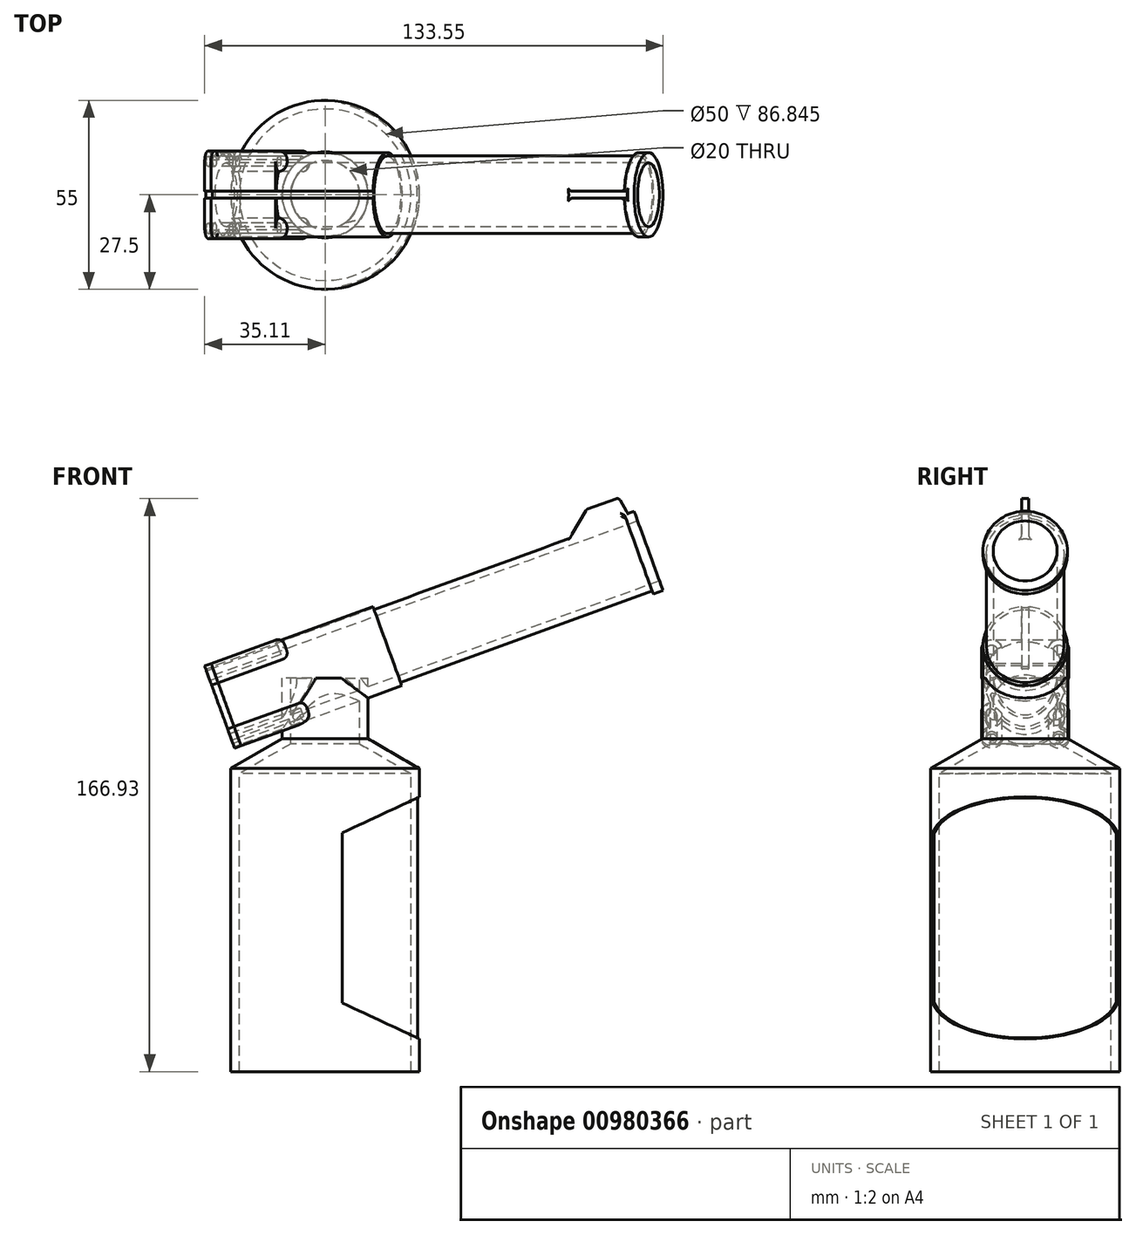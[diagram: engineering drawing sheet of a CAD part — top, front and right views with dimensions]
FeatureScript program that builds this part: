
annotation { "Feature Type Name" : "Feature", "Feature Type Description" : "" }
export const myFeature = defineFeature(function(context is Context, id is Id, definition is map)
    precondition{}
    {
        {
            var Q0;
            Q0=qCreatedBy(makeId("Front.planeOp"),FACE);
            var sketch = newSketch(context, id + "F0", { "sketchPlane" : qUnion([Q0])});
            skLineSegment(sketch, "E0", {"start": v(0, 0) * mm, "end": v(88.33, 32.15) * mm, "construction": true});
            skLineSegment(sketch, "E1", {"start": v(0, 151.2) * mm, "end": v(0, -135.9) * mm, "construction": true});
            skLineSegment(sketch, "E2", {"start": v(-3.08, 8.46) * mm, "end": v(85.25, 40.6) * mm, "construction": true});
            skLineSegment(sketch, "E3", {"start": v(85.25, 40.6) * mm, "end": v(91.4, 23.7) * mm, "construction": true});
            skLineSegment(sketch, "E4", {"start": v(91.4, 23.7) * mm, "end": v(3.08, -8.46) * mm, "construction": true});
            skLineSegment(sketch, "E5", {"start": v(3.08, -8.46) * mm, "end": v(-3.08, 8.46) * mm, "construction": true});
            skLineSegment(sketch, "E6", {"start": v(-52.04, -9.05) * mm, "end": v(68.24, 34.73) * mm});
            skLineSegment(sketch, "E7.0", {"start": v(-5.74, 9.93) * mm, "end": v(67.55, 36.61) * mm});
            skLineSegment(sketch, "E8", {"start": v(67.55, 36.61) * mm, "end": v(68.24, 34.73) * mm, "construction": true});
            skLineSegment(sketch, "E9", {"start": v(68.24, 34.73) * mm, "end": v(67.2, 37.55) * mm});
            skLineSegment(sketch, "E10", {"start": v(67.2, 37.55) * mm, "end": v(70.03, 38.58) * mm});
            skLineSegment(sketch, "E11", {"start": v(70.03, 38.58) * mm, "end": v(71.05, 35.76) * mm});
            skLineSegment(sketch, "E12", {"start": v(71.05, 35.76) * mm, "end": v(68.24, 34.73) * mm});
            skLineSegment(sketch, "E13", {"start": v(-5.74, 9.93) * mm, "end": v(-6.09, 10.87) * mm});
            skLineSegment(sketch, "E14", {"start": v(-6.09, 10.87) * mm, "end": v(-53.07, -6.23) * mm});
            skLineSegment(sketch, "E15", {"start": v(-53.07, -6.23) * mm, "end": v(-52.04, -9.05) * mm});
            skSolve(sketch);
        }
        {
            var Q0;
            Q0 = qSketchRegion(id + "F0", true);
            var Q1;
            Q1=sQuery(id+"F0.wireOp",EDGE,"E0");
            revolve(context, id + "F1", {"surfaceOperationType" : NewSurfaceOperationType.NEW, "entities" : qUnion([Q0]), "axis" : qUnion([Q1]), "revolveType" : RevolveType.FULL});
        }
        {
            var Q0;
            Q0=makeQuery(id+"F1.opRevolve","SWEPT_FACE",FACE,{"disambiguationData":[OSD([sQuery(id+"F0.wireOp",EDGE,"E15")])]});
            var sketch = newSketch(context, id + "F2", { "sketchPlane" : qUnion([Q0])});
            skCircle(sketch, "E16", {"center": v(-9.76, -9.76) * mm, "radius": 3 * mm});
            skCircle(sketch, "E17", {"center": v(9.76, -9.76) * mm, "radius": 3 * mm});
            skCircle(sketch, "E18", {"center": v(9.76, 9.76) * mm, "radius": 3 * mm});
            skCircle(sketch, "E19", {"center": v(-9.76, 9.76) * mm, "radius": 3 * mm});
            skLineSegment(sketch, "E20.bottom", {"start": v(-9.76, 9.76) * mm, "end": v(9.76, 9.76) * mm, "construction": true});
            skLineSegment(sketch, "E20.top", {"start": v(-9.76, -9.76) * mm, "end": v(9.76, -9.76) * mm, "construction": true});
            skLineSegment(sketch, "E20.left", {"start": v(-9.76, 9.76) * mm, "end": v(-9.76, -9.76) * mm, "construction": true});
            skLineSegment(sketch, "E20.right", {"start": v(9.76, 9.76) * mm, "end": v(9.76, -9.76) * mm, "construction": true});
            skCircle(sketch, "E21", {"center": v(0, 0) * mm, "radius": 10.8 * mm, "construction": true});
            skLineSegment(sketch, "E22", {"start": v(0, 12.3) * mm, "end": v(0, 9.3) * mm, "construction": true});
            skLineSegment(sketch, "E23", {"start": v(-9.76, 9.76) * mm, "end": v(9.76, -9.76) * mm, "construction": true});
            skCircle(sketch, "E24", {"center": v(-9.76, 9.76) * mm, "radius": 1.5 * mm});
            skCircle(sketch, "E25", {"center": v(-9.76, -9.76) * mm, "radius": 1.5 * mm});
            skCircle(sketch, "E26", {"center": v(9.76, -9.76) * mm, "radius": 1.5 * mm});
            skCircle(sketch, "E27", {"center": v(9.76, 9.76) * mm, "radius": 1.5 * mm});
            skLineSegment(sketch, "E28", {"start": v(-9.76, 12.76) * mm, "end": v(9.76, 12.76) * mm});
            skArc(sketch, "E29", {"start": v(7.64, 7.64) * mm, "mid": v(0, 10.8) * mm, "end": v(-7.64, 7.64) * mm});
            skSolve(sketch);
        }
        {
            var Q0;
            Q0 = qSketchRegion(id + "F2", true);
            extrude(context, id + "F3", {"entities" : qUnion([Q0]), "operationType" : NewBodyOperationType.ADD, "oppositeDirection" : true, "depth" : 20 * mm, "offsetDistance" : 25 * mm});
        }
        {
            var Q0;
            Q0=makeQuery(id+"F3.opExtrude","CAP_FACE",FACE,{"disambiguationData":[OSD([sQuery(id+"F2.wireOp",EDGE,"E18"),sQuery(id+"F2.wireOp",EDGE,"E19"),sQuery(id+"F2.wireOp",EDGE,"E24"),sQuery(id+"F2.wireOp",EDGE,"E27"),sQuery(id+"F2.wireOp",EDGE,"E28"),sQuery(id+"F2.wireOp",EDGE,"E29")])],"isStart":false});
            var sketch = newSketch(context, id + "F4", { "sketchPlane" : qUnion([Q0])});
            skCircle(sketch, "E30", {"center": v(-9.76, 9.76) * mm, "radius": 3 * mm});
            skCircle(sketch, "E31", {"center": v(9.76, 9.76) * mm, "radius": 3 * mm});
            skCircle(sketch, "E32", {"center": v(9.76, -9.76) * mm, "radius": 3 * mm});
            skCircle(sketch, "E33", {"center": v(-9.76, -9.76) * mm, "radius": 3 * mm});
            skSolve(sketch);
        }
        {
            var Q0;
            Q0 = qSketchRegion(id + "F4", true);
            extrude(context, id + "F5", {"entities" : qUnion([Q0]), "operationType" : NewBodyOperationType.ADD, "depth" : 2 * mm, "offsetDistance" : 25 * mm});
        }
        {
            var Q0;
            Q0=makeQuery(id+"F5.opExtrude","CAP_EDGE",EDGE,{"disambiguationData":[OSD([sQuery(id+"F4.wireOp",EDGE,"E31")])],"isStart":false});
            var Q1;
            Q1=makeQuery(id+"F5.opExtrude","CAP_EDGE",EDGE,{"disambiguationData":[OSD([sQuery(id+"F4.wireOp",EDGE,"E30")])],"isStart":false});
            var Q2;
            Q2=makeQuery(id+"F5.opExtrude","CAP_EDGE",EDGE,{"disambiguationData":[OSD([sQuery(id+"F4.wireOp",EDGE,"E33")])],"isStart":false});
            var Q3;
            Q3=makeQuery(id+"F5.opExtrude","CAP_EDGE",EDGE,{"disambiguationData":[OSD([sQuery(id+"F4.wireOp",EDGE,"E32")])],"isStart":false});
            fillet(context, id + "F6", {"entities" : qUnion([Q0, Q1, Q2, Q3]), "radius" : 2 * mm, "tangentPropagation" : true, "allowEdgeOverflow" : false});
        }
        {
            var Q0;
            Q0=makeQuery(id+"F3.boolean.opBoolean","MERGE",FACE,{"derivedFrom":[makeQuery(id+"F1.opRevolve","SWEPT_FACE",FACE,{"disambiguationData":[OSD([sQuery(id+"F0.wireOp",EDGE,"E15")])]}),makeQuery(id+"F3.opExtrude","CAP_FACE",FACE,{"disambiguationData":[OSD([sQuery(id+"F2.wireOp",EDGE,"E16"),sQuery(id+"F2.wireOp",EDGE,"E25")])],"isStart":true}),makeQuery(id+"F3.opExtrude","CAP_FACE",FACE,{"disambiguationData":[OSD([sQuery(id+"F2.wireOp",EDGE,"E17"),sQuery(id+"F2.wireOp",EDGE,"E26")])],"isStart":true}),makeQuery(id+"F3.opExtrude","CAP_FACE",FACE,{"disambiguationData":[OSD([sQuery(id+"F2.wireOp",EDGE,"E18"),sQuery(id+"F2.wireOp",EDGE,"E19"),sQuery(id+"F2.wireOp",EDGE,"E24"),sQuery(id+"F2.wireOp",EDGE,"E27"),sQuery(id+"F2.wireOp",EDGE,"E28"),sQuery(id+"F2.wireOp",EDGE,"E29")])],"isStart":true})]});
            var sketch = newSketch(context, id + "F7", { "sketchPlane" : qUnion([Q0])});
            skLineSegment(sketch, "E34.bottom", {"start": v(-1, 12.76) * mm, "end": v(1, 12.76) * mm});
            skLineSegment(sketch, "E34.top", {"start": v(-1, 11.76) * mm, "end": v(1, 11.76) * mm});
            skLineSegment(sketch, "E34.left", {"start": v(-1, 12.76) * mm, "end": v(-1, 11.76) * mm});
            skLineSegment(sketch, "E34.right", {"start": v(1, 12.76) * mm, "end": v(1, 11.76) * mm});
            skLineSegment(sketch, "E35", {"start": v(0, 0) * mm, "end": v(0, 12.76) * mm});
            skSolve(sketch);
        }
        {
            var Q0;
            Q0 = qSketchRegion(id + "F7", true);
            extrude(context, id + "F8", {"entities" : qUnion([Q0]), "operationType" : NewBodyOperationType.REMOVE, "oppositeDirection" : true, "depth" : 50 * mm, "offsetDistance" : 25 * mm});
        }
        {
            var Q0;
            Q0=makeQuery(id+"F8.boolean.opBoolean","INTERSECT",EDGE,{"derivedFrom":[makeQuery(id+"F1.opRevolve","SWEPT_FACE",FACE,{"disambiguationData":[OSD([sQuery(id+"F0.wireOp",EDGE,"E14")])]}),makeQuery(id+"F8.opExtrude","SWEPT_FACE",FACE,{"disambiguationData":[OSD([sQuery(id+"F7.wireOp",EDGE,"E34.right")])]})]});
            var Q1;
            Q1=makeQuery(id+"F8.boolean.opBoolean","COPY",EDGE,{"derivedFrom":makeQuery(id+"F8.opExtrude","SWEPT_EDGE",EDGE,{"disambiguationData":[OSD([sQuery(id+"F7.wireOp",EDGE,"E34.top"),sQuery(id+"F7.wireOp",EDGE,"E34.right")])]})});
            var Q2;
            Q2=makeQuery(id+"F8.boolean.opBoolean","COPY",EDGE,{"derivedFrom":makeQuery(id+"F8.opExtrude","SWEPT_EDGE",EDGE,{"disambiguationData":[OSD([sQuery(id+"F7.wireOp",EDGE,"E34.top"),sQuery(id+"F7.wireOp",EDGE,"E34.left")])]})});
            var Q3;
            Q3=makeQuery(id+"F8.boolean.opBoolean","INTERSECT",EDGE,{"derivedFrom":[makeQuery(id+"F1.opRevolve","SWEPT_FACE",FACE,{"disambiguationData":[OSD([sQuery(id+"F0.wireOp",EDGE,"E14")])]}),makeQuery(id+"F8.opExtrude","SWEPT_FACE",FACE,{"disambiguationData":[OSD([sQuery(id+"F7.wireOp",EDGE,"E34.left")])]})]});
            var Q4;
            Q4=makeQuery(id+"F8.boolean.opBoolean","COPY",EDGE,{"derivedFrom":makeQuery(id+"F8.opExtrude","SWEPT_EDGE",EDGE,{"disambiguationData":[OSD([sQuery(id+"F2.wireOp",EDGE,"E28"),sQuery(id+"F7.wireOp",EDGE,"E34.bottom"),sQuery(id+"F7.wireOp",EDGE,"E34.right")])]})});
            var Q5;
            Q5=makeQuery(id+"F8.boolean.opBoolean","COPY",EDGE,{"derivedFrom":makeQuery(id+"F8.opExtrude","SWEPT_EDGE",EDGE,{"disambiguationData":[OSD([sQuery(id+"F2.wireOp",EDGE,"E28"),sQuery(id+"F7.wireOp",EDGE,"E34.bottom"),sQuery(id+"F7.wireOp",EDGE,"E34.left")])]})});
            fillet(context, id + "F9", {"entities" : qUnion([Q0, Q1, Q2, Q3, Q4, Q5]), "radius" : 0.2 * mm, "tangentPropagation" : true, "allowEdgeOverflow" : false});
        }
        {
            var Q0;
            Q0=qCreatedBy(makeId("Front.planeOp"),FACE);
            var sketch = newSketch(context, id + "F10", { "sketchPlane" : qUnion([Q0])});
            skLineSegment(sketch, "E36", {"start": v(68.07, 38.1) * mm, "end": v(65.54, 42.5) * mm});
            skLineSegment(sketch, "E37", {"start": v(65.54, 42.5) * mm, "end": v(56.14, 39.08) * mm});
            skLineSegment(sketch, "E38", {"start": v(56.14, 39.08) * mm, "end": v(50.97, 30.12) * mm});
            skLineSegment(sketch, "E39", {"start": v(64.7, 43.61) * mm, "end": v(64.7, 37.15) * mm, "construction": true});
            skLineSegment(sketch, "E40", {"start": v(50.97, 30.12) * mm, "end": v(68.98, 36.24) * mm});
            skLineSegment(sketch, "E41", {"start": v(68.98, 36.24) * mm, "end": v(68.07, 38.1) * mm});
            skSolve(sketch);
        }
        {
            var Q0;
            Q0=makeQuery(id+"F10.imprint","IMPRINT",FACE,{"disambiguationData":[TD([[makeQuery(id+"F10.imprint","IMPRINT",EDGE,{"derivedFrom":sQuery(id+"F10.wireOp",EDGE,"E36")}),1.0]])]});
            extrude(context, id + "F11", {"entities" : qUnion([Q0]), "operationType" : NewBodyOperationType.ADD, "endBound" : BoundingType.SYMMETRIC, "depth" : 2 * mm, "offsetDistance" : 25 * mm});
        }
        {
            var Q0;
            Q0=makeQuery(id+"F11.opExtrude","SWEPT_EDGE",EDGE,{"disambiguationData":[OSD([sQuery(id+"F10.wireOp",EDGE,"E37"),sQuery(id+"F10.wireOp",EDGE,"E38")])]});
            var Q1;
            Q1=makeQuery(id+"F11.opExtrude","SWEPT_EDGE",EDGE,{"disambiguationData":[OSD([sQuery(id+"F10.wireOp",EDGE,"E36"),sQuery(id+"F10.wireOp",EDGE,"E37")])]});
            var Q2;
            Q2=makeQuery(id+"F11.boolean.opBoolean","INTERSECT",EDGE,{"derivedFrom":[makeQuery(id+"F1.opRevolve","SWEPT_FACE",FACE,{"disambiguationData":[OSD([sQuery(id+"F0.wireOp",EDGE,"E10")])]}),makeQuery(id+"F11.opExtrude","SWEPT_FACE",FACE,{"disambiguationData":[OSD([sQuery(id+"F10.wireOp",EDGE,"E36")])]})]});
            var Q3;
            Q3=makeQuery(id+"F11.boolean.opBoolean","INTERSECT",EDGE,{"derivedFrom":[makeQuery(id+"F1.opRevolve","SWEPT_FACE",FACE,{"disambiguationData":[OSD([sQuery(id+"F0.wireOp",EDGE,"E10")])]}),makeQuery(id+"F11.opExtrude","CAP_FACE",FACE,{"disambiguationData":[OSD([sQuery(id+"F10.wireOp",EDGE,"E36"),sQuery(id+"F10.wireOp",EDGE,"E37"),sQuery(id+"F10.wireOp",EDGE,"E38"),sQuery(id+"F10.wireOp",EDGE,"E40"),sQuery(id+"F10.wireOp",EDGE,"E41")])],"isStart":false})]});
            var Q4;
            Q4=makeQuery(id+"F11.boolean.opBoolean","INTERSECT",EDGE,{"derivedFrom":[makeQuery(id+"F1.opRevolve","SWEPT_FACE",FACE,{"disambiguationData":[OSD([sQuery(id+"F0.wireOp",EDGE,"E9")])]}),makeQuery(id+"F11.opExtrude","CAP_FACE",FACE,{"disambiguationData":[OSD([sQuery(id+"F10.wireOp",EDGE,"E36"),sQuery(id+"F10.wireOp",EDGE,"E37"),sQuery(id+"F10.wireOp",EDGE,"E38"),sQuery(id+"F10.wireOp",EDGE,"E40"),sQuery(id+"F10.wireOp",EDGE,"E41")])],"isStart":false})]});
            var Q5;
            Q5=makeQuery(id+"F11.boolean.opBoolean","INTERSECT",EDGE,{"derivedFrom":[makeQuery(id+"F1.opRevolve","SWEPT_FACE",FACE,{"disambiguationData":[OSD([sQuery(id+"F0.wireOp",EDGE,"E7.0")])]}),makeQuery(id+"F11.opExtrude","CAP_FACE",FACE,{"disambiguationData":[OSD([sQuery(id+"F10.wireOp",EDGE,"E36"),sQuery(id+"F10.wireOp",EDGE,"E37"),sQuery(id+"F10.wireOp",EDGE,"E38"),sQuery(id+"F10.wireOp",EDGE,"E40"),sQuery(id+"F10.wireOp",EDGE,"E41")])],"isStart":false})]});
            var Q6;
            Q6=makeQuery(id+"F11.boolean.opBoolean","INTERSECT",EDGE,{"derivedFrom":[makeQuery(id+"F1.opRevolve","SWEPT_FACE",FACE,{"disambiguationData":[OSD([sQuery(id+"F0.wireOp",EDGE,"E7.0")])]}),makeQuery(id+"F11.opExtrude","SWEPT_FACE",FACE,{"disambiguationData":[OSD([sQuery(id+"F10.wireOp",EDGE,"E38")])]})]});
            var Q7;
            Q7=makeQuery(id+"F11.boolean.opBoolean","INTERSECT",EDGE,{"derivedFrom":[makeQuery(id+"F1.opRevolve","SWEPT_FACE",FACE,{"disambiguationData":[OSD([sQuery(id+"F0.wireOp",EDGE,"E10")])]}),makeQuery(id+"F11.opExtrude","CAP_FACE",FACE,{"disambiguationData":[OSD([sQuery(id+"F10.wireOp",EDGE,"E36"),sQuery(id+"F10.wireOp",EDGE,"E37"),sQuery(id+"F10.wireOp",EDGE,"E38"),sQuery(id+"F10.wireOp",EDGE,"E40"),sQuery(id+"F10.wireOp",EDGE,"E41")])],"isStart":true})]});
            var Q8;
            Q8=makeQuery(id+"F11.boolean.opBoolean","INTERSECT",EDGE,{"derivedFrom":[makeQuery(id+"F1.opRevolve","SWEPT_FACE",FACE,{"disambiguationData":[OSD([sQuery(id+"F0.wireOp",EDGE,"E9")])]}),makeQuery(id+"F11.opExtrude","CAP_FACE",FACE,{"disambiguationData":[OSD([sQuery(id+"F10.wireOp",EDGE,"E36"),sQuery(id+"F10.wireOp",EDGE,"E37"),sQuery(id+"F10.wireOp",EDGE,"E38"),sQuery(id+"F10.wireOp",EDGE,"E40"),sQuery(id+"F10.wireOp",EDGE,"E41")])],"isStart":true})]});
            var Q9;
            Q9=makeQuery(id+"F11.boolean.opBoolean","INTERSECT",EDGE,{"derivedFrom":[makeQuery(id+"F1.opRevolve","SWEPT_FACE",FACE,{"disambiguationData":[OSD([sQuery(id+"F0.wireOp",EDGE,"E7.0")])]}),makeQuery(id+"F11.opExtrude","CAP_FACE",FACE,{"disambiguationData":[OSD([sQuery(id+"F10.wireOp",EDGE,"E36"),sQuery(id+"F10.wireOp",EDGE,"E37"),sQuery(id+"F10.wireOp",EDGE,"E38"),sQuery(id+"F10.wireOp",EDGE,"E40"),sQuery(id+"F10.wireOp",EDGE,"E41")])],"isStart":true})]});
            fillet(context, id + "F12", {"entities" : qUnion([Q0, Q1, Q2, Q3, Q4, Q5, Q6, Q7, Q8, Q9]), "radius" : 1 * mm, "tangentPropagation" : true, "allowEdgeOverflow" : false});
        }
        {
            var Q0;
            Q0=makeQuery(id+"F3.boolean.opBoolean","MERGE",FACE,{"derivedFrom":[makeQuery(id+"F1.opRevolve","SWEPT_FACE",FACE,{"disambiguationData":[OSD([sQuery(id+"F0.wireOp",EDGE,"E15")])]}),makeQuery(id+"F3.opExtrude","CAP_FACE",FACE,{"disambiguationData":[OSD([sQuery(id+"F2.wireOp",EDGE,"E16"),sQuery(id+"F2.wireOp",EDGE,"E25")])],"isStart":true}),makeQuery(id+"F3.opExtrude","CAP_FACE",FACE,{"disambiguationData":[OSD([sQuery(id+"F2.wireOp",EDGE,"E17"),sQuery(id+"F2.wireOp",EDGE,"E26")])],"isStart":true}),makeQuery(id+"F3.opExtrude","CAP_FACE",FACE,{"disambiguationData":[OSD([sQuery(id+"F2.wireOp",EDGE,"E18"),sQuery(id+"F2.wireOp",EDGE,"E19"),sQuery(id+"F2.wireOp",EDGE,"E24"),sQuery(id+"F2.wireOp",EDGE,"E27"),sQuery(id+"F2.wireOp",EDGE,"E28"),sQuery(id+"F2.wireOp",EDGE,"E29")])],"isStart":true})]});
            var sketch = newSketch(context, id + "F13", { "sketchPlane" : qUnion([Q0])});
            skArc(sketch, "E42.0", {"start": v(-9.76, 12.76) * mm, "mid": v(-12.75, 10) * mm, "end": v(-10.25, 6.8) * mm});
            skArc(sketch, "E42.1", {"start": v(-10.25, 6.8) * mm, "mid": v(-12.3, 0) * mm, "end": v(-10.25, -6.8) * mm});
            skArc(sketch, "E42.2", {"start": v(-10.25, -6.8) * mm, "mid": v(-11.88, -11.88) * mm, "end": v(-6.8, -10.25) * mm});
            skArc(sketch, "E42.3", {"start": v(-6.8, -10.25) * mm, "mid": v(0, -12.3) * mm, "end": v(6.8, -10.25) * mm});
            skArc(sketch, "E42.4", {"start": v(6.8, -10.25) * mm, "mid": v(11.88, -11.88) * mm, "end": v(10.25, -6.8) * mm});
            skLineSegment(sketch, "E42.5", {"start": v(-0.8, 11.76) * mm, "end": v(0.8, 11.76) * mm});
            skArc(sketch, "E42.6", {"start": v(-0.8, 11.76) * mm, "mid": v(-0.94, 11.82) * mm, "end": v(-1, 11.96) * mm});
            skLineSegment(sketch, "E42.7", {"start": v(-1, 12.56) * mm, "end": v(-1, 11.96) * mm});
            skArc(sketch, "E42.8", {"start": v(-1, 12.56) * mm, "mid": v(-1.06, 12.7) * mm, "end": v(-1.2, 12.76) * mm});
            skArc(sketch, "E42.9", {"start": v(1, 11.96) * mm, "mid": v(0.94, 11.82) * mm, "end": v(0.8, 11.76) * mm});
            skLineSegment(sketch, "E42.10", {"start": v(1, 12.56) * mm, "end": v(1, 11.96) * mm});
            skArc(sketch, "E42.11", {"start": v(1.2, 12.76) * mm, "mid": v(1.06, 12.7) * mm, "end": v(1, 12.56) * mm});
            skLineSegment(sketch, "E42.12", {"start": v(1.2, 12.76) * mm, "end": v(9.76, 12.76) * mm});
            skArc(sketch, "E42.13", {"start": v(10.25, 6.8) * mm, "mid": v(12.75, 10) * mm, "end": v(9.76, 12.76) * mm});
            skLineSegment(sketch, "E42.14", {"start": v(-9.76, 12.76) * mm, "end": v(-1.2, 12.76) * mm});
            skArc(sketch, "E42.15", {"start": v(10.25, -6.8) * mm, "mid": v(12.3, 0) * mm, "end": v(10.25, 6.8) * mm});
            skCircle(sketch, "E43.0", {"center": v(-9.76, 9.76) * mm, "radius": 1.5 * mm});
            skCircle(sketch, "E44.0", {"center": v(-9.76, -9.76) * mm, "radius": 1.5 * mm});
            skCircle(sketch, "E45.0", {"center": v(9.76, -9.76) * mm, "radius": 1.5 * mm});
            skCircle(sketch, "E46.0", {"center": v(9.76, 9.76) * mm, "radius": 1.5 * mm});
            skSolve(sketch);
        }
        {
            var Q0;
            Q0 = qSketchRegion(id + "F13", true);
            extrude(context, id + "F14", {"entities" : qUnion([Q0]), "depth" : 2 * mm, "offsetDistance" : 25 * mm});
        }
        {
            var Q0;
            Q0=qCreatedBy(makeId("Front.planeOp"),FACE);
            var sketch = newSketch(context, id + "F15", { "sketchPlane" : qUnion([Q0])});
            skLineSegment(sketch, "E47", {"start": v(-47, -36.66) * mm, "end": v(-47, -124.66) * mm});
            skLineSegment(sketch, "E48", {"start": v(-47, -36.66) * mm, "end": v(-32, -28) * mm});
            skLineSegment(sketch, "E49", {"start": v(-32, -28) * mm, "end": v(-32, -10) * mm});
            skLineSegment(sketch, "E50", {"start": v(-20, 26.98) * mm, "end": v(-20, -72) * mm, "construction": true});
            skLineSegment(sketch, "E51.0", {"start": v(-30, -29.15) * mm, "end": v(-30, -10) * mm});
            skLineSegment(sketch, "E51.1", {"start": v(-45, -37.81) * mm, "end": v(-30, -29.15) * mm});
            skLineSegment(sketch, "E51.2", {"start": v(-45, -37.81) * mm, "end": v(-45, -124.66) * mm});
            skLineSegment(sketch, "E52", {"start": v(-30, -10) * mm, "end": v(-32, -10) * mm});
            skLineSegment(sketch, "E53", {"start": v(-45, -124.66) * mm, "end": v(-47, -124.66) * mm});
            skLineSegment(sketch, "E54.0", {"start": v(-47.5, -36.37) * mm, "end": v(-47.5, -124.66) * mm});
            skLineSegment(sketch, "E54.1", {"start": v(-47.5, -36.37) * mm, "end": v(-32.5, -27.71) * mm});
            skLineSegment(sketch, "E54.2", {"start": v(-32.5, -27.71) * mm, "end": v(-32.5, -10) * mm});
            skLineSegment(sketch, "E55", {"start": v(-47.5, -124.66) * mm, "end": v(-47, -124.66) * mm});
            skLineSegment(sketch, "E56", {"start": v(-32, -10) * mm, "end": v(-32.5, -10) * mm});
            skSolve(sketch);
        }
        {
            var Q0;
            Q0=makeQuery(id+"F15.imprint","IMPRINT",FACE,{"disambiguationData":[TD([[makeQuery(id+"F15.imprint","IMPRINT",EDGE,{"derivedFrom":sQuery(id+"F15.wireOp",EDGE,"E47")}),-1.0]])]});
            var Q1;
            Q1=sQuery(id+"F15.wireOp",EDGE,"E50");
            revolve(context, id + "F16", {"operationType" : NewBodyOperationType.ADD, "surfaceOperationType" : NewSurfaceOperationType.NEW, "entities" : qUnion([Q0]), "axis" : qUnion([Q1]), "revolveType" : RevolveType.FULL});
        }
        {
            var Q0;
            Q0=qCreatedBy(makeId("Front.planeOp"),FACE);
            var sketch = newSketch(context, id + "F17", { "sketchPlane" : qUnion([Q0])});
            skLineSegment(sketch, "E57", {"start": v(29.6, -34.31) * mm, "end": v(-15, -55.11) * mm});
            skLineSegment(sketch, "E58", {"start": v(-15, -55.11) * mm, "end": v(-15, -104.66) * mm});
            skLineSegment(sketch, "E59", {"start": v(-15, -104.66) * mm, "end": v(29.6, -125.46) * mm});
            skLineSegment(sketch, "E60", {"start": v(29.6, -125.46) * mm, "end": v(29.6, -34.31) * mm});
            skSolve(sketch);
        }
        {
            var Q0;
            Q0 = qSketchRegion(id + "F17", true);
            extrude(context, id + "F18", {"entities" : qUnion([Q0]), "operationType" : NewBodyOperationType.REMOVE, "endBound" : BoundingType.SYMMETRIC, "oppositeDirection" : true, "depth" : 128 * mm, "offsetDistance" : 25 * mm});
        }
        {
            var Q0;
            Q0=makeQuery(id+"F15.imprint","IMPRINT",FACE,{"disambiguationData":[TD([[makeQuery(id+"F15.imprint","IMPRINT",EDGE,{"derivedFrom":sQuery(id+"F15.wireOp",EDGE,"E47")}),1.0]])]});
            var Q1;
            Q1=sQuery(id+"F15.wireOp",EDGE,"E50");
            revolve(context, id + "F19", {"operationType" : NewBodyOperationType.ADD, "surfaceOperationType" : NewSurfaceOperationType.NEW, "entities" : qUnion([Q0]), "axis" : qUnion([Q1]), "revolveType" : RevolveType.FULL});
        }
    });
